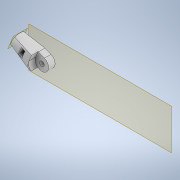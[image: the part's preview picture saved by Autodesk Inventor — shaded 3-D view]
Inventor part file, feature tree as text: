
AUTODESK INVENTOR PART (.ipt)
format: ipt  version: 2021 (Build 250183000, 183)  size: 213,504 bytes
history: native  units: mm
features: sketch x6, extrude x4, other x4, plane x2, reference x2, loft x1, hole x1, projected_geometry x1
ambient origin geometry x8: Origin, YZ Plane, XZ Plane, XY Plane, X Axis, Y Axis, Z Axis, Center Point
bodies: Solid1 (feature_tree)
feature tree (21):
  plane  "Work Plane1"
  extrude  "Extrusion1"  Depth=10.0mm TaperAngle=0.0deg
  plane  "Work Plane2"
  loft  "Loft1"
  extrude  "Extrusion3"  TaperAngle=0.0deg  [1 undecoded]
  extrude  "Extrusion4"  Depth=5.0mm TaperAngle=0.0deg
  hole  "Hole1"  [1 undecoded]
  extrude  "Extrusion5"  Depth=2.0mm
  sketch  "Sketch1"  dims[d1=3.5mm d3=10.0mm d4=0.0mm]
  reference  "Reference1"
  reference  "Reference2"
  sketch  "Sketch3"  dims[d10=5.0mm d11=15.0mm]
  projected_geometry  "Projected Loop1"
  other  "Edges1"
  sketch  "Sketch5"  dims[d12=0.0mm d13=90.0deg d14=0.0mm d15=90.0deg]
  sketch  "Sketch6"  dims[d18=10.5mm d19=5.0mm d20=0.0mm]
  sketch  "Sketch7"  dims[d21=7.0mm d22=3.0mm]
  sketch  "Sketch8"  dims[d23=6.0mm d24=2.0mm d25=9.0mm d26=0.0mm d27=3.5mm d28=6.0mm d29=4.0mm d30=2.0mm d31=90.0deg d32=8.0mm d33=20.594885mm d34=5.0mm d35=0.0mm d5=0.5mm d6=0.872665mm]
  parser-record x1  (decoder bookkeeping rows leaked as tree rows — omitted from the tree; the rows remain in map.json)
  other  "Assembly.iam"
  other  "LRS-50-Series(MW):1"
note: 2 required parameter values undecoded (feature->parameter linkage not recoverable at this tier; creation-order binding heuristic only, values carry confidence <= 0.55)
note: 1 file-system path scrubbed to <path> (originals preserved in map.json)
